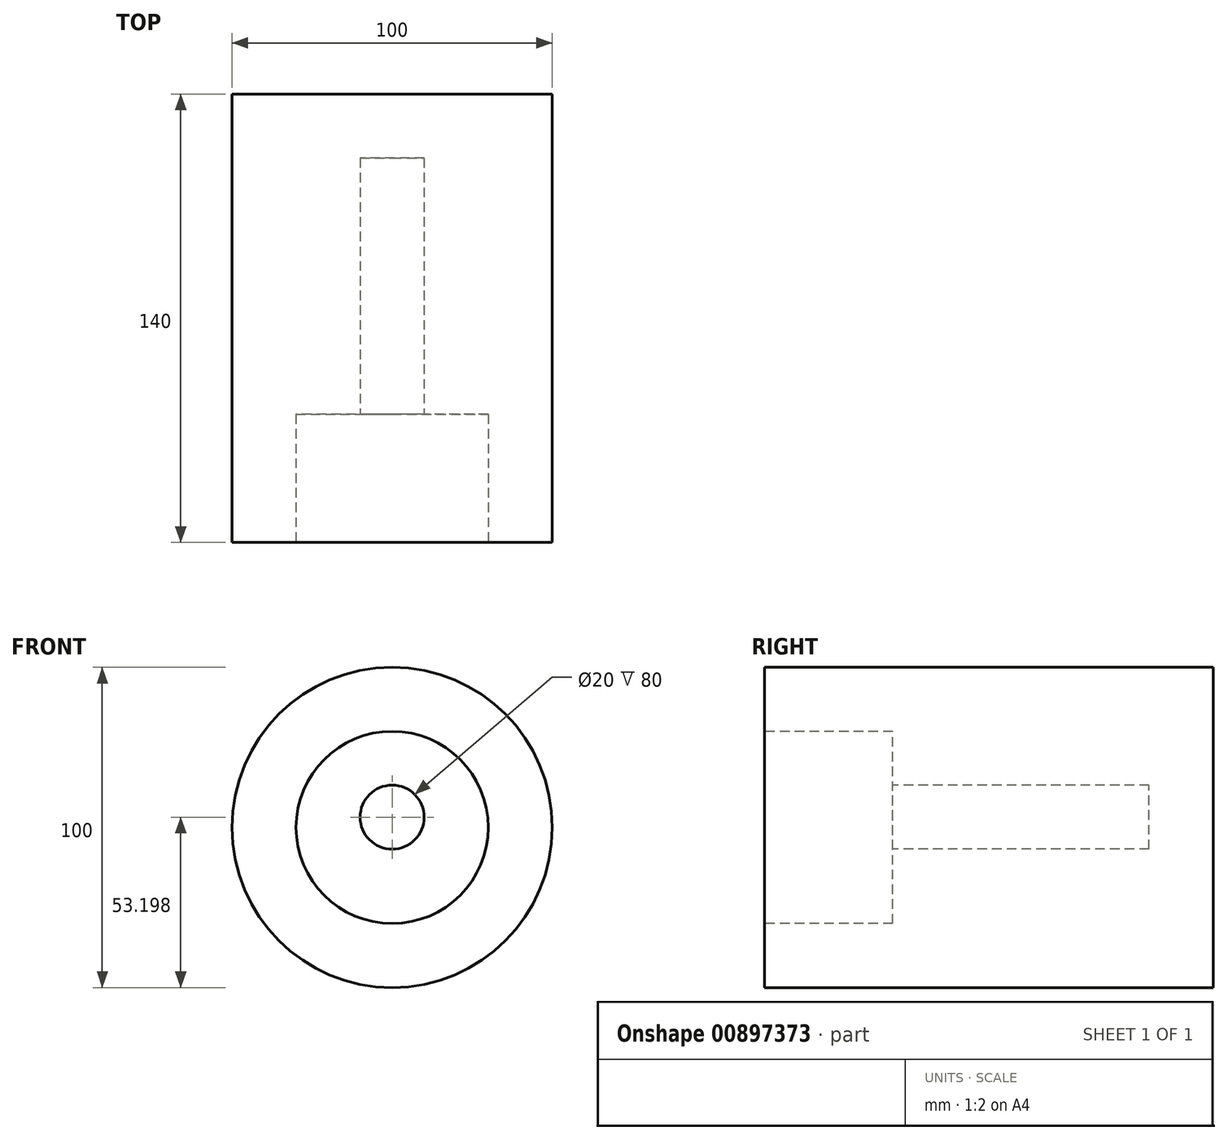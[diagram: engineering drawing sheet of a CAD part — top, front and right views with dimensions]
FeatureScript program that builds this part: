
annotation { "Feature Type Name" : "Feature", "Feature Type Description" : "" }
export const myFeature = defineFeature(function(context is Context, id is Id, definition is map)
    precondition{}
    {
        {
            var Q0;
            Q0=qCreatedBy(makeId("Front.planeOp"),FACE);
            var sketch = newSketch(context, id + "F0", { "sketchPlane" : qUnion([Q0])});
            skCircle(sketch, "E0", {"center": v(0, 0) * mm, "radius": 50 * mm});
            skSolve(sketch);
        }
        {
            var Q0;
            Q0=makeQuery(id+"F0.imprint","IMPRINT",FACE,{"disambiguationData":[TD([[makeQuery(id+"F0.imprint","IMPRINT",EDGE,{"derivedFrom":sQuery(id+"F0.wireOp",EDGE,"E0")}),1.0]])]});
            extrude(context, id + "F1", {"entities" : qUnion([Q0]), "depth" : 140 * mm, "offsetDistance" : 25.4 * mm});
        }
        {
            var Q0;
            Q0=makeQuery(id+"F1.opExtrude","CAP_FACE",FACE,{"disambiguationData":[OSD([sQuery(id+"F0.wireOp",EDGE,"E0")])],"isStart":false});
            var sketch = newSketch(context, id + "F2", { "sketchPlane" : qUnion([Q0])});
            skCircle(sketch, "E1", {"center": v(0, 0) * mm, "radius": 30 * mm});
            skSolve(sketch);
        }
        {
            var Q0;
            Q0=makeQuery(id+"F2.imprint","IMPRINT",FACE,{"disambiguationData":[TD([[makeQuery(id+"F2.imprint","IMPRINT",EDGE,{"derivedFrom":sQuery(id+"F2.wireOp",EDGE,"E1")}),1.0]])]});
            extrude(context, id + "F3", {"entities" : qUnion([Q0]), "operationType" : NewBodyOperationType.REMOVE, "oppositeDirection" : true, "depth" : 40 * mm, "offsetDistance" : 25.4 * mm});
        }
        {
            var Q0;
            Q0=makeQuery(id+"F3.boolean.opBoolean","COPY",FACE,{"derivedFrom":makeQuery(id+"F3.opExtrude","CAP_FACE",FACE,{"disambiguationData":[OSD([sQuery(id+"F2.wireOp",EDGE,"E1")])],"isStart":false})});
            var sketch = newSketch(context, id + "F4", { "sketchPlane" : qUnion([Q0])});
            skCircle(sketch, "E2", {"center": v(0, 3.2) * mm, "radius": 10 * mm});
            skSolve(sketch);
        }
        {
            var Q0;
            Q0=makeQuery(id+"F4.imprint","IMPRINT",FACE,{"disambiguationData":[TD([[makeQuery(id+"F4.imprint","IMPRINT",EDGE,{"derivedFrom":sQuery(id+"F4.wireOp",EDGE,"E2")}),1.0]])]});
            extrude(context, id + "F5", {"entities" : qUnion([Q0]), "operationType" : NewBodyOperationType.REMOVE, "oppositeDirection" : true, "depth" : 80 * mm, "offsetDistance" : 25.4 * mm});
        }
    });
